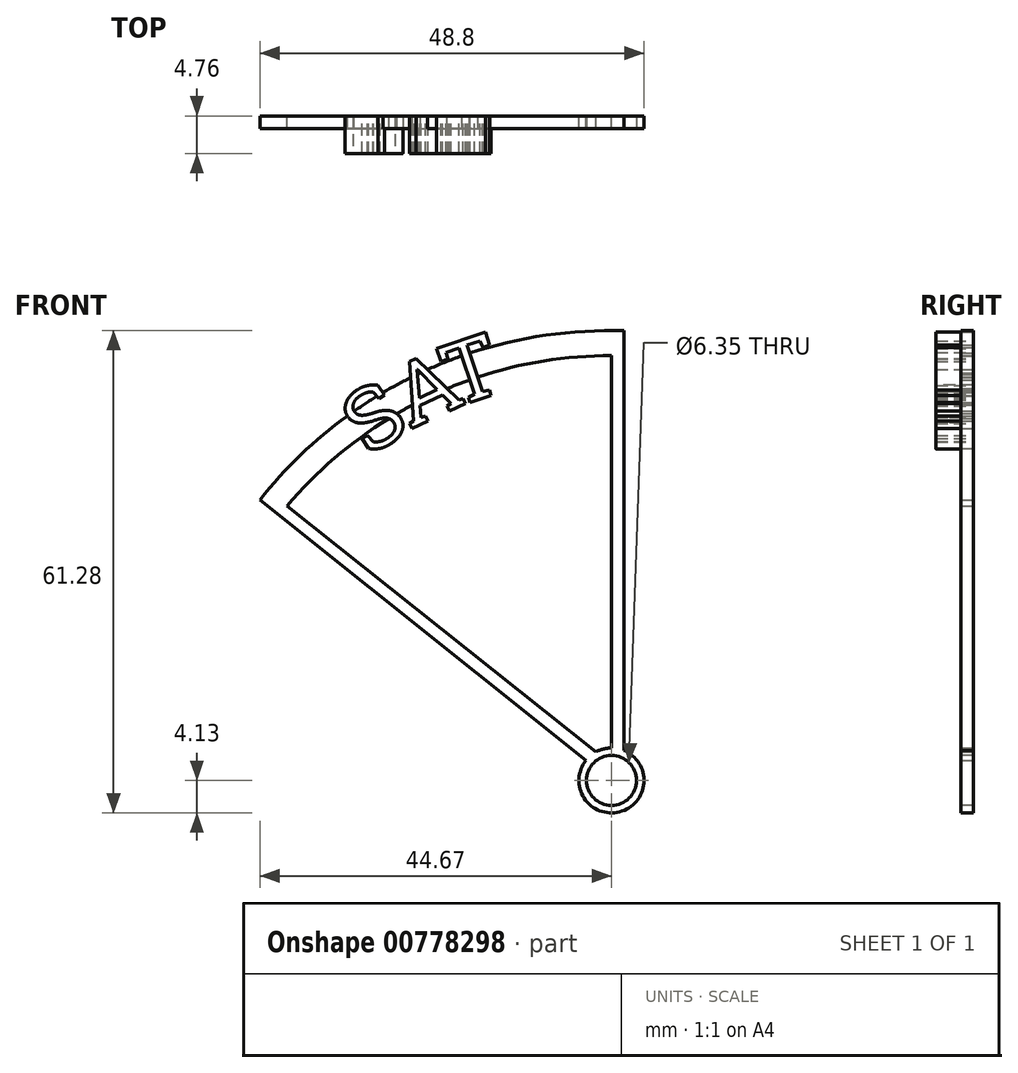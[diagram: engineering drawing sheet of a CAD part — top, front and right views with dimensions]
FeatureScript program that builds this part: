
annotation { "Feature Type Name" : "Feature", "Feature Type Description" : "" }
export const myFeature = defineFeature(function(context is Context, id is Id, definition is map)
    precondition{}
    {
        {
            var Q0;
            Q0=qCreatedBy(makeId("Front.planeOp"),FACE);
            var sketch = newSketch(context, id + "F0", { "sketchPlane" : qUnion([Q0])});
            skCircle(sketch, "E0", {"center": v(0, 0) * mm, "radius": 59.18 * mm, "construction": true});
            skCircle(sketch, "E1", {"center": v(0, 0) * mm, "radius": 50.8 * mm, "construction": true});
            skLineSegment(sketch, "E2", {"start": v(0, 0) * mm, "end": v(0, 59.18) * mm, "construction": true});
            skLineSegment(sketch, "E3", {"start": v(0, 0) * mm, "end": v(-46.3, 36.86) * mm, "construction": true});
            skLineSegment(sketch, "E4", {"start": v(0, 0) * mm, "end": v(-32.36, 49.55) * mm, "construction": true});
            skLineSegment(sketch, "E5", {"start": v(0, 0) * mm, "end": v(-25.15, 53.57) * mm, "construction": true});
            skLineSegment(sketch, "E6", {"start": v(0, 0) * mm, "end": v(-18.92, 56.08) * mm, "construction": true});
            skText(sketch, "E7", { "text": "S", "fontName": "RobotoSlab-Regular.ttf"});
            skText(sketch, "E8", { "text": "A", "fontName": "RobotoSlab-Regular.ttf"});
            skText(sketch, "E9", { "text": "T", "fontName": "RobotoSlab-Regular.ttf"});
            skLineSegment(sketch, "E10", {"start": v(0, 0) * mm, "end": v(-35.24, 47.67) * mm, "construction": true});
            skLineSegment(sketch, "E11", {"start": v(0, 0) * mm, "end": v(-15.42, 57.26) * mm, "construction": true});
            skLineSegment(sketch, "E12", {"start": v(0, 0) * mm, "end": v(-0.06, 59.18) * mm, "construction": true});
            const initialGuessF0  = {"E7": [-0.0309, 0.04103, 0.8373, 0.54675, 0.00794], "E8": [-0.02561, 0.04459, 0.90524, 0.4249, 0.00794], "E9": [-0.01989, 0.04737, 0.94752, 0.3197, 0.00794]};
            skSetInitialGuess(sketch, initialGuessF0);
            skSolve(sketch);
        }
        {
            var Q0;
            Q0=qSketchRegion(id+"F0",true);
            extrude(context, id + "F1", {"entities" : qUnion([Q0]), "depth" : 4.76 * mm, "offsetDistance" : 25.4 * mm});
        }
        {
            var Q0;
            Q0=qCreatedBy(makeId("Front.planeOp"),FACE);
            var sketch = newSketch(context, id + "F2", { "sketchPlane" : qUnion([Q0])});
            skCircle(sketch, "E13", {"center": v(0, 0) * mm, "radius": 53.98 * mm, "construction": true});
            skLineSegment(sketch, "E14", {"start": v(0, 0) * mm, "end": v(0, 53.98) * mm, "construction": true});
            skLineSegment(sketch, "E15", {"start": v(0, 53.98) * mm, "end": v(0, 0) * mm, "construction": true});
            skLineSegment(sketch, "E16", {"start": v(0, 0) * mm, "end": v(-44.67, 35.64) * mm, "construction": true});
            skCircle(sketch, "E17", {"center": v(0, 0) * mm, "radius": 57.14 * mm, "construction": true});
            skLineSegment(sketch, "E18", {"start": v(0, 0) * mm, "end": v(0, -53.98) * mm, "construction": true});
            skCircle(sketch, "E19", {"center": v(0, 0) * mm, "radius": 4.13 * mm, "construction": true});
            skLineSegment(sketch, "E20", {"start": v(-41.19, 34.89) * mm, "end": v(-1.99, 3.62) * mm, "construction": true});
            skLineSegment(sketch, "E21", {"start": v(1.59, 57.12) * mm, "end": v(1.59, 3.8) * mm, "construction": true});
            skLineSegment(sketch, "E22", {"start": v(-44.67, 35.64) * mm, "end": v(-3.23, 2.57) * mm});
            skLineSegment(sketch, "E23", {"start": v(1.59, 57.12) * mm, "end": v(1.59, 3.8) * mm});
            skLineSegment(sketch, "E24", {"start": v(0, 53.98) * mm, "end": v(0, 4.13) * mm});
            skLineSegment(sketch, "E25", {"start": v(-41.19, 34.89) * mm, "end": v(-1.99, 3.62) * mm});
            skCircle(sketch, "E26", {"center": v(0, 0) * mm, "radius": 4.13 * mm});
            skArc(sketch, "E27", {"start": v(0, 53.97) * mm, "mid": v(-22.7, 48.97) * mm, "end": v(-41.19, 34.89) * mm});
            skArc(sketch, "E28", {"start": v(1.59, 57.12) * mm, "mid": v(-24.09, 51.86) * mm, "end": v(-44.67, 35.64) * mm});
            skSolve(sketch);
        }
        {
            var Q0;
            {var subQ3=sQuery(id+"F2.wireOp",EDGE,"E22");Q0=makeQuery(id+"F2.imprint","IMPRINT",FACE,{"disambiguationData":[TD([[makeQuery(id+"F2.imprint","IMPRINT",EDGE,{"derivedFrom":subQ3}),1.0]])]});}
            var Q1;
            {var subQ0=sQuery(id+"F2.wireOp",EDGE,"E26");var subQ1=makeQuery(id+"F2.imprint","INTERSECT",VERTEX,{"derivedFrom":[sQuery(id+"F2.wireOp",EDGE,"E23"),subQ0]});Q1=makeQuery(id+"F2.imprint","IMPRINT",FACE,{"disambiguationData":[TD([[makeQuery(id+"F2.imprint","IMPRINT",EDGE,{"disambiguationData":[TD([[subQ1,-1.0]])],"derivedFrom":subQ0}),1.0]])]});}
            extrude(context, id + "F3", {"entities" : qUnion([Q0, Q1]), "operationType" : NewBodyOperationType.ADD, "depth" : 1.59 * mm, "offsetDistance" : 25.4 * mm});
        }
        {
            var Q0;
            {var subQ0=sQuery(id+"F2.wireOp",EDGE,"E25");var subQ1=sQuery(id+"F2.wireOp",EDGE,"E24");var subQ2=sQuery(id+"F2.wireOp",EDGE,"E22");var subQ3=sQuery(id+"F2.wireOp",EDGE,"E23");var subQ4=sQuery(id+"F2.wireOp",EDGE,"E26");var subQ5=sQuery(id+"F2.wireOp",EDGE,"E27");var subQ6=sQuery(id+"F2.wireOp",EDGE,"E28");Q0=makeQuery(id+"F3.boolean.opBoolean","SPLIT",FACE,{"disambiguationData":[TD([makeQuery(id+"F1.opExtrude","SWEPT_FACE",FACE,{"disambiguationData":[OSD([sQuery(id+"F0.wireOp",EDGE,"E7.sketch_text.stroke-21")])]})])],"derivedFrom":makeQuery(id+"F3.opExtrude","CAP_FACE",FACE,{"disambiguationData":[OSD([subQ2,subQ3,subQ1,subQ0,subQ4,subQ5,subQ6])],"isStart":false})});}
            var sketch = newSketch(context, id + "F4", { "sketchPlane" : qUnion([Q0])});
            skPoint(sketch, "E29", {"position": v(0, 0) * mm});
            skSolve(sketch);
        }
        {
            var Q0;
            Q0=sQuery(id+"F4.wireOp",VERTEX,"E29");
            var Q1;
            Q1=makeQuery(id+"F1.opExtrude","SWEPT_BODY",BODY,{"disambiguationData":[OSD([sQuery(id+"F0.wireOp",EDGE,"E7.sketch_text.stroke-0"),sQuery(id+"F0.wireOp",EDGE,"E7.sketch_text.stroke-1"),sQuery(id+"F0.wireOp",EDGE,"E7.sketch_text.stroke-2"),sQuery(id+"F0.wireOp",EDGE,"E7.sketch_text.stroke-3"),sQuery(id+"F0.wireOp",EDGE,"E7.sketch_text.stroke-4"),sQuery(id+"F0.wireOp",EDGE,"E7.sketch_text.stroke-5"),sQuery(id+"F0.wireOp",EDGE,"E7.sketch_text.stroke-6"),sQuery(id+"F0.wireOp",EDGE,"E7.sketch_text.stroke-7"),sQuery(id+"F0.wireOp",EDGE,"E7.sketch_text.stroke-8"),sQuery(id+"F0.wireOp",EDGE,"E7.sketch_text.stroke-9"),sQuery(id+"F0.wireOp",EDGE,"E7.sketch_text.stroke-10"),sQuery(id+"F0.wireOp",EDGE,"E7.sketch_text.stroke-11"),sQuery(id+"F0.wireOp",EDGE,"E7.sketch_text.stroke-12"),sQuery(id+"F0.wireOp",EDGE,"E7.sketch_text.stroke-13"),sQuery(id+"F0.wireOp",EDGE,"E7.sketch_text.stroke-14"),sQuery(id+"F0.wireOp",EDGE,"E7.sketch_text.stroke-15"),sQuery(id+"F0.wireOp",EDGE,"E7.sketch_text.stroke-16"),sQuery(id+"F0.wireOp",EDGE,"E7.sketch_text.stroke-17"),sQuery(id+"F0.wireOp",EDGE,"E7.sketch_text.stroke-18"),sQuery(id+"F0.wireOp",EDGE,"E7.sketch_text.stroke-19"),sQuery(id+"F0.wireOp",EDGE,"E7.sketch_text.stroke-20"),sQuery(id+"F0.wireOp",EDGE,"E7.sketch_text.stroke-21"),sQuery(id+"F0.wireOp",EDGE,"E7.sketch_text.stroke-22"),sQuery(id+"F0.wireOp",EDGE,"E7.sketch_text.stroke-23"),sQuery(id+"F0.wireOp",EDGE,"E7.sketch_text.stroke-24"),sQuery(id+"F0.wireOp",EDGE,"E7.sketch_text.stroke-25"),sQuery(id+"F0.wireOp",EDGE,"E7.sketch_text.stroke-26"),sQuery(id+"F0.wireOp",EDGE,"E7.sketch_text.stroke-27"),sQuery(id+"F0.wireOp",EDGE,"E7.sketch_text.stroke-28"),sQuery(id+"F0.wireOp",EDGE,"E7.sketch_text.stroke-29")])]});
            hole(context, id + "F5", {"style" : HoleStyle.SIMPLE, "endStyle" : HoleEndStyle.THROUGH, "holeDiameter" : 6.35 * mm, "majorDiameter" : 6.35 * mm, "isTappedThrough" : true, "tappedDepth" : 12.7 * mm, "tapClearance" : 3, "locations" : qUnion([Q0]), "scope" : qUnion([Q1])});
        }
    });
